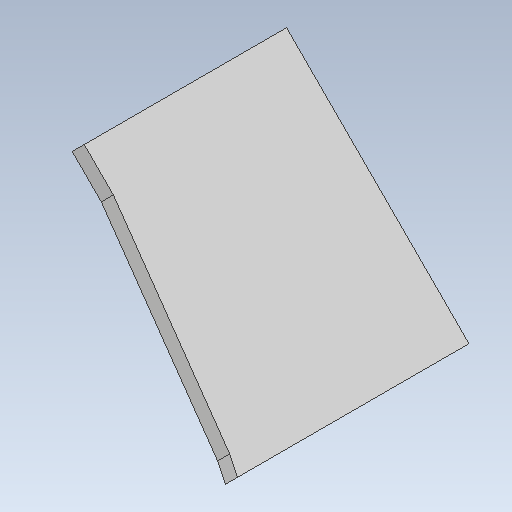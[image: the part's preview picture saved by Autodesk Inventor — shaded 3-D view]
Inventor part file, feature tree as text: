
AUTODESK INVENTOR PART (.ipt)
format: ipt  version: 2020 (Build 240168000, 168)  size: 109,056 bytes
history: native  units: mm
features: other x9, extrude x3, sketch x3
ambient origin geometry x8: Origin, YZ Plane, XZ Plane, XY Plane, X Axis, Y Axis, Z Axis, Center Point
bodies: Body1 (feature_tree)
feature tree (15):
  other  "Sólido1"
  extrude  "Extrusão1"  TaperAngle=45.0deg  [1 undecoded]
  extrude  "Extrusão2"  Depth=3.0mm TaperAngle=0.0deg
  extrude  "Extrusão3"  Depth=35.6mm TaperAngle=0.0deg
  sketch  "Esboço1"  dims[d0=3.0mm d1=45.0deg]
  other  "Referência1"
  sketch  "Esboço3"  dims[d2=3.0mm d3=11.5mm d4=0.0mm]
  sketch  "Esboço6"  dims[d5=35.6mm d6=0.0mm d7=19.0mm d8=0.0mm]
  other  "Referência4"
  other  "Referência5"
  other  "Referência6"
  other  "<userpath>\Desktop\rabo\3d\ela.iam"
  other  "ela.iam"
  other  "lateral_V2:1"
  other  "tampa:1"
note: 1 required parameter value undecoded (feature->parameter linkage not recoverable at this tier; creation-order binding heuristic only, values carry confidence <= 0.55)
